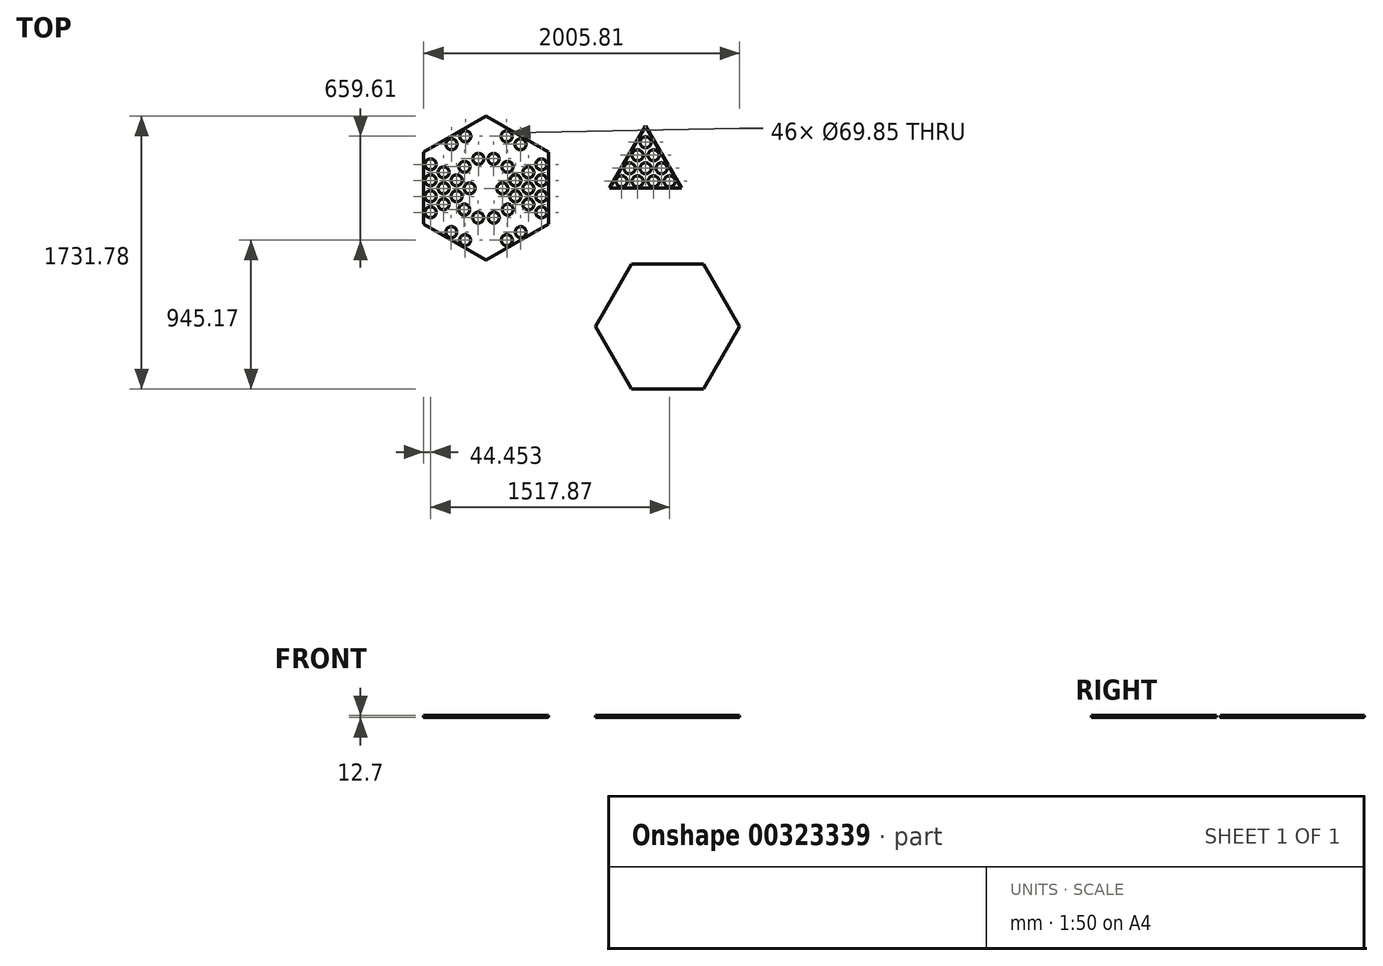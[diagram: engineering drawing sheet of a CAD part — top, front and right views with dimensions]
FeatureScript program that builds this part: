
annotation { "Feature Type Name" : "Feature", "Feature Type Description" : "" }
export const myFeature = defineFeature(function(context is Context, id is Id, definition is map)
    precondition{}
    {
        {
            var Q0;
            Q0=qCreatedBy(makeId("Top.planeOp"),FACE);
            var sketch = newSketch(context, id + "F0", { "sketchPlane" : qUnion([Q0])});
            skCircle(sketch, "E0.cCircle", {"center": v(1013.19, 131.98) * mm, "radius": 131.98 * mm, "construction": true});
            skLineSegment(sketch, "E0.0", {"start": v(1241.79, 0) * mm, "end": v(784.59, 0) * mm});
            skLineSegment(sketch, "E0.1", {"start": v(784.59, 0) * mm, "end": v(1013.19, 395.95) * mm});
            skLineSegment(sketch, "E0.2", {"start": v(1013.19, 395.95) * mm, "end": v(1241.79, 0) * mm});
            skPoint(sketch, "E0.0.midPoint", {"position": v(1013.19, 0) * mm});
            skLineSegment(sketch, "E1", {"start": v(784.59, 0) * mm, "end": v(861.58, 44.45) * mm});
            skCircle(sketch, "E2", {"center": v(861.58, 44.45) * mm, "radius": 34.93 * mm});
            skLineSegment(sketch, "E3", {"start": v(1241.79, 0) * mm, "end": v(1164.8, 44.45) * mm});
            skCircle(sketch, "E4.1.0.0", {"center": v(963.18, 44.45) * mm, "radius": 34.93 * mm});
            skCircle(sketch, "E4.2.0.0", {"center": v(1064.78, 44.45) * mm, "radius": 34.93 * mm});
            skCircle(sketch, "E4.3.0.0", {"center": v(1166.38, 44.45) * mm, "radius": 34.93 * mm});
            skLineSegment(sketch, "E4.direction1", {"start": v(861.58, 44.45) * mm, "end": v(963.18, 44.45) * mm, "construction": true});
            skLineSegment(sketch, "E5", {"start": v(912.38, 44.45) * mm, "end": v(912.38, 127) * mm, "construction": true});
            skCircle(sketch, "E6", {"center": v(912.38, 127) * mm, "radius": 34.93 * mm});
            skCircle(sketch, "E7.1.0.0", {"center": v(1013.98, 127) * mm, "radius": 34.93 * mm});
            skCircle(sketch, "E7.2.0.0", {"center": v(1115.58, 127) * mm, "radius": 34.93 * mm});
            skLineSegment(sketch, "E7.direction1", {"start": v(912.38, 127) * mm, "end": v(1013.98, 127) * mm, "construction": true});
            skLineSegment(sketch, "E8", {"start": v(963.18, 127) * mm, "end": v(963.18, 209.55) * mm});
            skCircle(sketch, "E9", {"center": v(963.18, 209.55) * mm, "radius": 34.93 * mm});
            skCircle(sketch, "E10.1.0.0", {"center": v(1064.78, 209.55) * mm, "radius": 34.93 * mm});
            skLineSegment(sketch, "E10.direction1", {"start": v(963.18, 209.55) * mm, "end": v(1064.78, 209.55) * mm, "construction": true});
            skLineSegment(sketch, "E11", {"start": v(1013.98, 209.55) * mm, "end": v(1013.98, 292.1) * mm});
            skCircle(sketch, "E12", {"center": v(1013.98, 292.1) * mm, "radius": 34.93 * mm});
            skCircle(sketch, "E13.cCircle", {"center": v(0, 0) * mm, "radius": 457.2 * mm, "construction": true});
            skLineSegment(sketch, "E13.0", {"start": v(0, -457.2) * mm, "end": v(-395.95, -228.6) * mm});
            skLineSegment(sketch, "E13.1", {"start": v(-395.95, -228.6) * mm, "end": v(-395.95, 228.6) * mm});
            skLineSegment(sketch, "E13.2", {"start": v(-395.95, 228.6) * mm, "end": v(0, 457.2) * mm});
            skLineSegment(sketch, "E13.3", {"start": v(0, 457.2) * mm, "end": v(395.95, 228.6) * mm});
            skLineSegment(sketch, "E13.4", {"start": v(395.95, 228.6) * mm, "end": v(395.95, -228.6) * mm});
            skLineSegment(sketch, "E13.5", {"start": v(395.95, -228.6) * mm, "end": v(0, -457.2) * mm});
            skLineSegment(sketch, "E14", {"start": v(-395.95, -228.6) * mm, "end": v(395.95, 228.6) * mm});
            skLineSegment(sketch, "E15", {"start": v(395.95, -228.6) * mm, "end": v(-395.95, 228.6) * mm});
            skLineSegment(sketch, "E16", {"start": v(0, -457.2) * mm, "end": v(0, 457.2) * mm});
            skCircle(sketch, "E17", {"center": v(351.5, -153.19) * mm, "radius": 34.93 * mm});
            skCircle(sketch, "E18.0.1.0", {"center": v(351.5, -51.59) * mm, "radius": 34.93 * mm});
            skCircle(sketch, "E18.0.2.0", {"center": v(351.5, 50.01) * mm, "radius": 34.93 * mm});
            skCircle(sketch, "E18.0.3.0", {"center": v(351.5, 151.61) * mm, "radius": 34.93 * mm});
            skCircle(sketch, "E19", {"center": v(268.95, -102.39) * mm, "radius": 34.93 * mm});
            skCircle(sketch, "E20.0.1.0", {"center": v(268.95, -0.79) * mm, "radius": 34.93 * mm});
            skCircle(sketch, "E20.0.2.0", {"center": v(268.95, 100.81) * mm, "radius": 34.93 * mm});
            skCircle(sketch, "E21", {"center": v(186.4, -51.59) * mm, "radius": 34.93 * mm});
            skCircle(sketch, "E22.0.1.0", {"center": v(186.4, 50.01) * mm, "radius": 34.93 * mm});
            skCircle(sketch, "E23", {"center": v(103.85, -0.79) * mm, "radius": 34.93 * mm});
            skCircle(sketch, "E24.MirrorC", {"center": v(-103.85, -0.79) * mm, "radius": 34.93 * mm});
            skCircle(sketch, "E25.MirrorC", {"center": v(-186.4, -51.59) * mm, "radius": 34.93 * mm});
            skCircle(sketch, "E26.MirrorC", {"center": v(-186.4, 50.01) * mm, "radius": 34.93 * mm});
            skCircle(sketch, "E27.MirrorC", {"center": v(-268.95, 100.81) * mm, "radius": 34.93 * mm});
            skCircle(sketch, "E28.MirrorC", {"center": v(-268.95, -0.79) * mm, "radius": 34.93 * mm});
            skCircle(sketch, "E29.MirrorC", {"center": v(-268.95, -102.39) * mm, "radius": 34.93 * mm});
            skCircle(sketch, "E30.MirrorC", {"center": v(-351.5, -153.19) * mm, "radius": 34.93 * mm});
            skCircle(sketch, "E31.MirrorC", {"center": v(-351.5, -51.59) * mm, "radius": 34.93 * mm});
            skCircle(sketch, "E32.MirrorC", {"center": v(-351.5, 151.61) * mm, "radius": 34.93 * mm});
            skCircle(sketch, "E33.MirrorC", {"center": v(-351.5, 50.01) * mm, "radius": 34.93 * mm});
            skCircle(sketch, "E34.MirrorC", {"center": v(136.5, 136.42) * mm, "radius": 34.93 * mm});
            skCircle(sketch, "E35.MirrorC", {"center": v(48.52, 187.22) * mm, "radius": 34.93 * mm});
            skCircle(sketch, "E36.MirrorC", {"center": v(131.07, 330.2) * mm, "radius": 34.93 * mm});
            skCircle(sketch, "E37.MirrorC", {"center": v(219.06, 279.4) * mm, "radius": 34.93 * mm});
            skCircle(sketch, "E38.MirrorC", {"center": v(-49.89, -186.43) * mm, "radius": 34.93 * mm});
            skCircle(sketch, "E39.MirrorC", {"center": v(-132.44, -329.41) * mm, "radius": 34.93 * mm});
            skCircle(sketch, "E40.MirrorC", {"center": v(-220.43, -278.61) * mm, "radius": 34.93 * mm});
            skCircle(sketch, "E41.MirrorC", {"center": v(-137.88, -135.63) * mm, "radius": 34.93 * mm});
            skCircle(sketch, "E42.MirrorC", {"center": v(137.88, -135.63) * mm, "radius": 34.93 * mm});
            skCircle(sketch, "E43.MirrorC", {"center": v(49.89, -186.43) * mm, "radius": 34.93 * mm});
            skCircle(sketch, "E44.MirrorC", {"center": v(132.44, -329.41) * mm, "radius": 34.93 * mm});
            skCircle(sketch, "E45.MirrorC", {"center": v(220.43, -278.61) * mm, "radius": 34.93 * mm});
            skCircle(sketch, "E46.MirrorC", {"center": v(-136.5, 136.42) * mm, "radius": 34.93 * mm});
            skCircle(sketch, "E47.MirrorC", {"center": v(-48.52, 187.22) * mm, "radius": 34.93 * mm});
            skCircle(sketch, "E48.MirrorC", {"center": v(-131.07, 330.2) * mm, "radius": 34.93 * mm});
            skCircle(sketch, "E49.MirrorC", {"center": v(-219.06, 279.4) * mm, "radius": 34.93 * mm});
            skSolve(sketch);
        }
        {
            var Q0;
            Q0 = qSketchRegion(id + "F0", true);
            extrude(context, id + "F1", {"entities" : qUnion([Q0]), "depth" : 12.7 * mm});
        }
        {
            var Q0;
            Q0=qCreatedBy(makeId("Top.planeOp"),FACE);
            var sketch = newSketch(context, id + "F2", { "sketchPlane" : qUnion([Q0])});
            skCircle(sketch, "E50.cCircle", {"center": v(1152.66, -878.63) * mm, "radius": 395.95 * mm, "construction": true});
            skLineSegment(sketch, "E50.0", {"start": v(1381.26, -1274.58) * mm, "end": v(924.06, -1274.58) * mm});
            skLineSegment(sketch, "E50.1", {"start": v(924.06, -1274.58) * mm, "end": v(695.46, -878.63) * mm});
            skLineSegment(sketch, "E50.2", {"start": v(695.46, -878.63) * mm, "end": v(924.06, -482.68) * mm});
            skLineSegment(sketch, "E50.3", {"start": v(924.06, -482.68) * mm, "end": v(1381.26, -482.68) * mm});
            skLineSegment(sketch, "E50.4", {"start": v(1381.26, -482.68) * mm, "end": v(1609.86, -878.63) * mm});
            skLineSegment(sketch, "E50.5", {"start": v(1609.86, -878.63) * mm, "end": v(1381.26, -1274.58) * mm});
            skPoint(sketch, "E50.0.midPoint", {"position": v(1152.66, -1274.58) * mm});
            skSolve(sketch);
        }
        {
            var Q0;
            Q0 = qSketchRegion(id + "F2", true);
            extrude(context, id + "F3", {"entities" : qUnion([Q0]), "depth" : 12.7 * mm});
        }
        {
            var Q0;
            Q0=makeQuery(id+"F1.opExtrude","CAP_FACE",FACE,{"disambiguationData":[OSD([sQuery(id+"F0.wireOp",EDGE,"E13.0"),sQuery(id+"F0.wireOp",EDGE,"E13.1"),sQuery(id+"F0.wireOp",EDGE,"E13.2"),sQuery(id+"F0.wireOp",EDGE,"E13.3"),sQuery(id+"F0.wireOp",EDGE,"E13.4"),sQuery(id+"F0.wireOp",EDGE,"E13.5"),sQuery(id+"F0.wireOp",EDGE,"E17"),sQuery(id+"F0.wireOp",EDGE,"E18.0.1.0"),sQuery(id+"F0.wireOp",EDGE,"E18.0.2.0"),sQuery(id+"F0.wireOp",EDGE,"E18.0.3.0"),sQuery(id+"F0.wireOp",EDGE,"E19"),sQuery(id+"F0.wireOp",EDGE,"E20.0.1.0"),sQuery(id+"F0.wireOp",EDGE,"E20.0.2.0"),sQuery(id+"F0.wireOp",EDGE,"E21"),sQuery(id+"F0.wireOp",EDGE,"E22.0.1.0"),sQuery(id+"F0.wireOp",EDGE,"E23"),sQuery(id+"F0.wireOp",EDGE,"E24.MirrorC"),sQuery(id+"F0.wireOp",EDGE,"E25.MirrorC"),sQuery(id+"F0.wireOp",EDGE,"E26.MirrorC"),sQuery(id+"F0.wireOp",EDGE,"E27.MirrorC"),sQuery(id+"F0.wireOp",EDGE,"E28.MirrorC"),sQuery(id+"F0.wireOp",EDGE,"E29.MirrorC"),sQuery(id+"F0.wireOp",EDGE,"E30.MirrorC"),sQuery(id+"F0.wireOp",EDGE,"E31.MirrorC"),sQuery(id+"F0.wireOp",EDGE,"E32.MirrorC"),sQuery(id+"F0.wireOp",EDGE,"E33.MirrorC"),sQuery(id+"F0.wireOp",EDGE,"E34.MirrorC"),sQuery(id+"F0.wireOp",EDGE,"E35.MirrorC"),sQuery(id+"F0.wireOp",EDGE,"E36.MirrorC"),sQuery(id+"F0.wireOp",EDGE,"E37.MirrorC"),sQuery(id+"F0.wireOp",EDGE,"E38.MirrorC"),sQuery(id+"F0.wireOp",EDGE,"E39.MirrorC"),sQuery(id+"F0.wireOp",EDGE,"E40.MirrorC"),sQuery(id+"F0.wireOp",EDGE,"E41.MirrorC"),sQuery(id+"F0.wireOp",EDGE,"E42.MirrorC"),sQuery(id+"F0.wireOp",EDGE,"E43.MirrorC"),sQuery(id+"F0.wireOp",EDGE,"E44.MirrorC"),sQuery(id+"F0.wireOp",EDGE,"E45.MirrorC"),sQuery(id+"F0.wireOp",EDGE,"E46.MirrorC"),sQuery(id+"F0.wireOp",EDGE,"E47.MirrorC"),sQuery(id+"F0.wireOp",EDGE,"E48.MirrorC"),sQuery(id+"F0.wireOp",EDGE,"E49.MirrorC")])],"isStart":true});
            fillet(context, id + "F4", {"entities" : qUnion([Q0]), "radius" : 5.08 * mm, "tangentPropagation" : true, "allowEdgeOverflow" : false});
        }
    });
